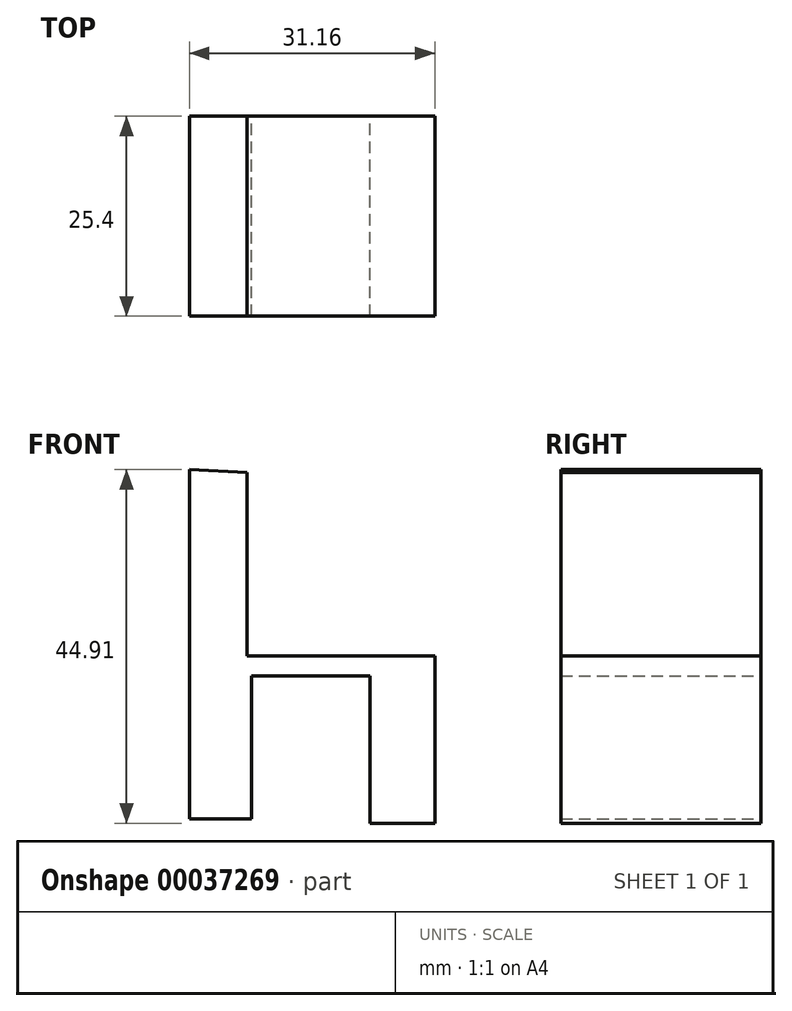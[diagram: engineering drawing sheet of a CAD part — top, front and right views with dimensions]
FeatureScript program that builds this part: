
annotation { "Feature Type Name" : "Feature", "Feature Type Description" : "" }
export const myFeature = defineFeature(function(context is Context, id is Id, definition is map)
    precondition{}
    {
        {
            var Q0;
            Q0=qCreatedBy(makeId("Front.planeOp"),FACE);
            var sketch = newSketch(context, id + "F0", { "sketchPlane" : qUnion([Q0])});
            skLineSegment(sketch, "E0", {"start": v(-66.9, 57.65) * mm, "end": v(-66.9, 13.29) * mm});
            skLineSegment(sketch, "E1", {"start": v(-66.9, 13.29) * mm, "end": v(-59.02, 13.29) * mm});
            skLineSegment(sketch, "E2", {"start": v(-59.02, 13.29) * mm, "end": v(-59.02, 31.44) * mm});
            skLineSegment(sketch, "E3", {"start": v(-59.02, 31.44) * mm, "end": v(-44, 31.44) * mm});
            skLineSegment(sketch, "E4", {"start": v(-44, 31.44) * mm, "end": v(-44, 12.74) * mm});
            skLineSegment(sketch, "E5", {"start": v(-44, 12.74) * mm, "end": v(-35.74, 12.74) * mm});
            skLineSegment(sketch, "E6", {"start": v(-35.74, 12.74) * mm, "end": v(-35.74, 34) * mm});
            skLineSegment(sketch, "E7", {"start": v(-35.74, 34) * mm, "end": v(-59.57, 34) * mm});
            skLineSegment(sketch, "E8", {"start": v(-59.57, 34) * mm, "end": v(-59.57, 57.28) * mm});
            skLineSegment(sketch, "E9", {"start": v(-59.57, 57.28) * mm, "end": v(-66.9, 57.65) * mm});
            skSolve(sketch);
        }
        {
            var Q0;
            Q0 = qSketchRegion(id + "F0", true);
            extrude(context, id + "F1", {"entities" : qUnion([Q0]), "depth" : 25.4 * mm});
        }
    });
